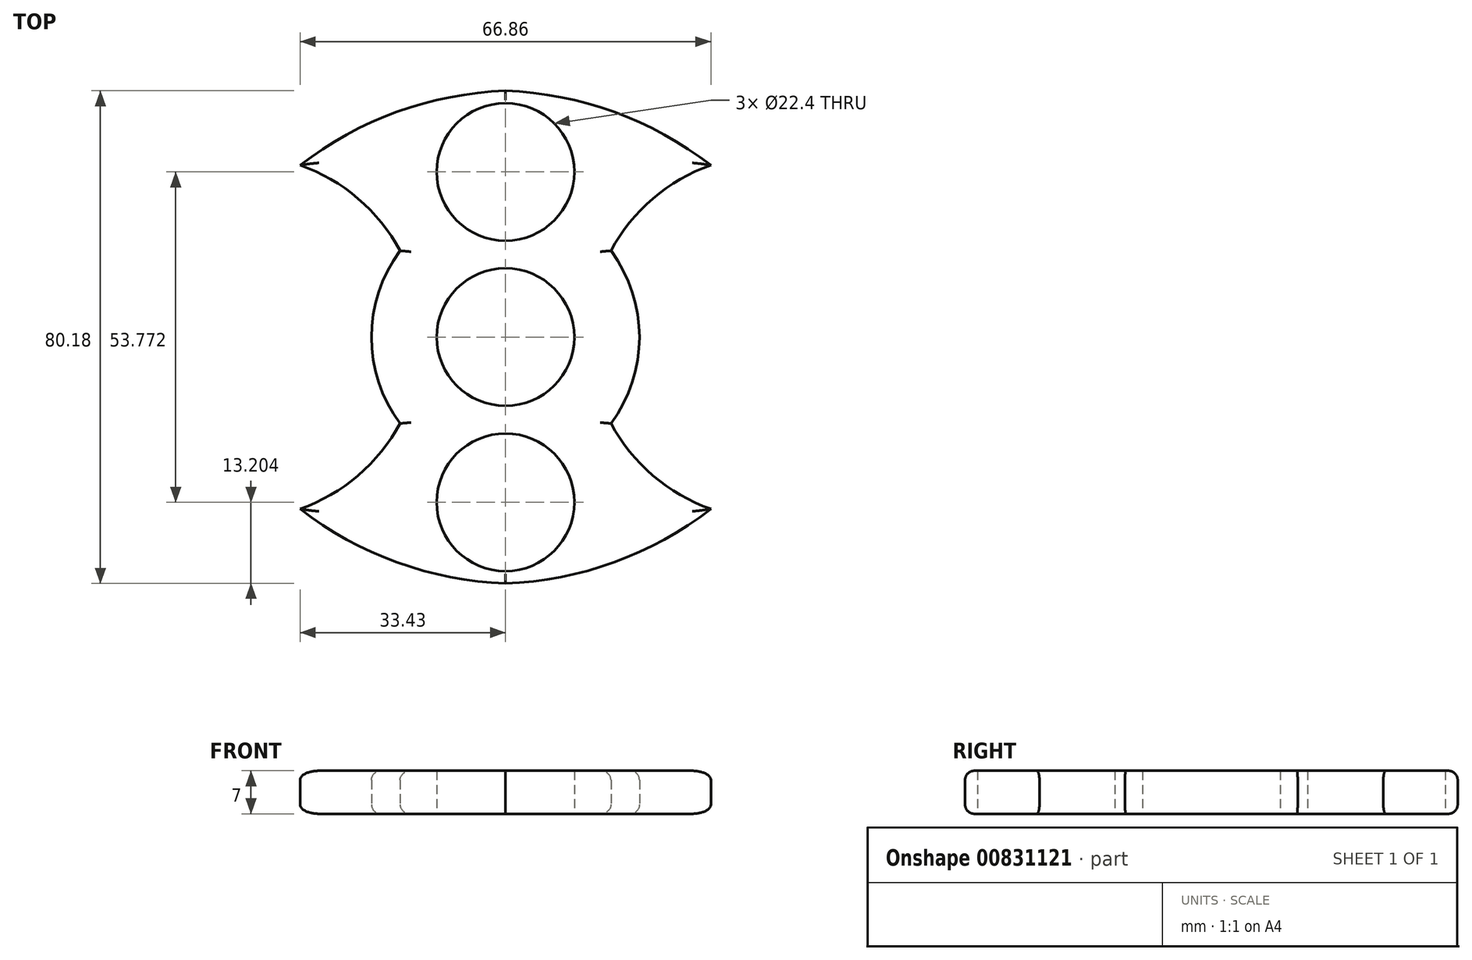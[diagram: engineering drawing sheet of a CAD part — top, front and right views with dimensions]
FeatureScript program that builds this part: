
annotation { "Feature Type Name" : "Feature", "Feature Type Description" : "" }
export const myFeature = defineFeature(function(context is Context, id is Id, definition is map)
    precondition{}
    {
        {
            var Q0;
            Q0=qCreatedBy(makeId("Top.planeOp"),FACE);
            var sketch = newSketch(context, id + "F0", { "sketchPlane" : qUnion([Q0])});
            skCircle(sketch, "E0", {"center": v(0, 0) * mm, "radius": 11.2 * mm});
            skCircle(sketch, "E1", {"center": v(0, 26.89) * mm, "radius": 11.2 * mm});
            skCircle(sketch, "E2.1.1", {"center": v(0, -26.89) * mm, "radius": 11.2 * mm});
            skArc(sketch, "E3", {"start": v(33.43, 27.98) * mm, "mid": v(17.67, 36.66) * mm, "end": v(0, 40.09) * mm});
            skArc(sketch, "E4.MirrorCS", {"start": v(-33.43, 27.98) * mm, "mid": v(-17.67, 36.66) * mm, "end": v(0, 40.09) * mm});
            skArc(sketch, "E5.MirrorCS", {"start": v(-33.43, -27.98) * mm, "mid": v(-17.67, -36.66) * mm, "end": v(0, -40.09) * mm});
            skArc(sketch, "E6.MirrorCS", {"start": v(33.43, -27.98) * mm, "mid": v(17.67, -36.66) * mm, "end": v(0, -40.09) * mm});
            skArc(sketch, "E7", {"start": v(33.43, 27.98) * mm, "mid": v(24, 22.53) * mm, "end": v(17.16, 14.05) * mm});
            skArc(sketch, "E8.MirrorCS", {"start": v(-33.43, 27.98) * mm, "mid": v(-24, 22.53) * mm, "end": v(-17.16, 14.05) * mm});
            skArc(sketch, "E9.trimOffspring", {"start": v(1.21, 40.03) * mm, "mid": v(0, 40.09) * mm, "end": v(-1.21, 40.03) * mm});
            skPoint(sketch, "E10.orphan", {"position": v(10.5, 8) * mm});
            skPoint(sketch, "E11.orphan", {"position": v(-10.5, 8) * mm});
            skPoint(sketch, "E12.start.orphan", {"position": v(11.11, 19.76) * mm});
            skPoint(sketch, "E13.start.orphan", {"position": v(-11.11, 19.76) * mm});
            skPoint(sketch, "E14.orphan", {"position": v(-10.5, -8) * mm});
            skPoint(sketch, "E15.orphan", {"position": v(10.5, -8) * mm});
            skPoint(sketch, "E16.MirrorCS.start.orphan", {"position": v(11.11, -19.76) * mm});
            skPoint(sketch, "E17.MirrorCS.start.orphan", {"position": v(-11.11, -19.76) * mm});
            skArc(sketch, "E18.trimOffspring", {"start": v(-1.21, -40.03) * mm, "mid": v(0, -40.09) * mm, "end": v(1.21, -40.03) * mm});
            skArc(sketch, "E19", {"start": v(17.16, -14.05) * mm, "mid": v(21.8, 0) * mm, "end": v(17.16, 14.05) * mm});
            skArc(sketch, "E20.MirrorCS", {"start": v(-17.16, -14.05) * mm, "mid": v(-21.8, 0) * mm, "end": v(-17.16, 14.05) * mm});
            skArc(sketch, "E21.trimOffspring", {"start": v(17.16, -14.05) * mm, "mid": v(24, -22.53) * mm, "end": v(33.43, -27.98) * mm});
            skArc(sketch, "E22.trimOffspring", {"start": v(-17.16, -14.05) * mm, "mid": v(-24, -22.53) * mm, "end": v(-33.43, -27.98) * mm});
            skSolve(sketch);
        }
        {
            var Q0;
            Q0=makeQuery(id+"F0.imprint","IMPRINT",FACE,{"disambiguationData":[TD([[makeQuery(id+"F0.imprint","IMPRINT",EDGE,{"derivedFrom":sQuery(id+"F0.wireOp",EDGE,"E0")}),-1.0]])]});
            extrude(context, id + "F1", {"entities" : qUnion([Q0]), "depth" : 7 * mm, "offsetDistance" : 25 * mm});
        }
        {
            var Q0;
            Q0=makeQuery(id+"F1.opExtrude","CAP_EDGE",EDGE,{"disambiguationData":[OSD([sQuery(id+"F0.wireOp",EDGE,"E4.MirrorCS")])],"isStart":false});
            var Q1;
            Q1=makeQuery(id+"F1.opExtrude","CAP_EDGE",EDGE,{"disambiguationData":[OSD([sQuery(id+"F0.wireOp",EDGE,"E3")])],"isStart":false});
            var Q2;
            Q2=makeQuery(id+"F1.opExtrude","CAP_EDGE",EDGE,{"disambiguationData":[OSD([sQuery(id+"F0.wireOp",EDGE,"E8.MirrorCS")])],"isStart":false});
            var Q3;
            Q3=makeQuery(id+"F1.opExtrude","CAP_EDGE",EDGE,{"disambiguationData":[OSD([sQuery(id+"F0.wireOp",EDGE,"E20.MirrorCS")])],"isStart":false});
            var Q4;
            Q4=makeQuery(id+"F1.opExtrude","CAP_EDGE",EDGE,{"disambiguationData":[OSD([sQuery(id+"F0.wireOp",EDGE,"E22.trimOffspring")])],"isStart":false});
            var Q5;
            Q5=makeQuery(id+"F1.opExtrude","CAP_EDGE",EDGE,{"disambiguationData":[OSD([sQuery(id+"F0.wireOp",EDGE,"E5.MirrorCS")])],"isStart":false});
            var Q6;
            Q6=makeQuery(id+"F1.opExtrude","CAP_EDGE",EDGE,{"disambiguationData":[OSD([sQuery(id+"F0.wireOp",EDGE,"E6.MirrorCS")])],"isStart":false});
            var Q7;
            Q7=makeQuery(id+"F1.opExtrude","CAP_EDGE",EDGE,{"disambiguationData":[OSD([sQuery(id+"F0.wireOp",EDGE,"E21.trimOffspring")])],"isStart":false});
            var Q8;
            Q8=makeQuery(id+"F1.opExtrude","CAP_EDGE",EDGE,{"disambiguationData":[OSD([sQuery(id+"F0.wireOp",EDGE,"E19")])],"isStart":false});
            var Q9;
            Q9=makeQuery(id+"F1.opExtrude","CAP_EDGE",EDGE,{"disambiguationData":[OSD([sQuery(id+"F0.wireOp",EDGE,"E7")])],"isStart":false});
            fillet(context, id + "F2", {"entities" : qUnion([Q0, Q1, Q2, Q3, Q4, Q5, Q6, Q7, Q8, Q9]), "radius" : 1.5 * mm, "tangentPropagation" : true, "allowEdgeOverflow" : false});
        }
        {
            var Q0;
            Q0=makeQuery(id+"F1.opExtrude","CAP_EDGE",EDGE,{"disambiguationData":[OSD([sQuery(id+"F0.wireOp",EDGE,"E3")])],"isStart":true});
            var Q1;
            Q1=makeQuery(id+"F1.opExtrude","CAP_EDGE",EDGE,{"disambiguationData":[OSD([sQuery(id+"F0.wireOp",EDGE,"E4.MirrorCS")])],"isStart":true});
            var Q2;
            Q2=makeQuery(id+"F1.opExtrude","CAP_EDGE",EDGE,{"disambiguationData":[OSD([sQuery(id+"F0.wireOp",EDGE,"E8.MirrorCS")])],"isStart":true});
            var Q3;
            Q3=makeQuery(id+"F1.opExtrude","CAP_EDGE",EDGE,{"disambiguationData":[OSD([sQuery(id+"F0.wireOp",EDGE,"E20.MirrorCS")])],"isStart":true});
            var Q4;
            Q4=makeQuery(id+"F1.opExtrude","CAP_EDGE",EDGE,{"disambiguationData":[OSD([sQuery(id+"F0.wireOp",EDGE,"E22.trimOffspring")])],"isStart":true});
            var Q5;
            Q5=makeQuery(id+"F1.opExtrude","CAP_EDGE",EDGE,{"disambiguationData":[OSD([sQuery(id+"F0.wireOp",EDGE,"E5.MirrorCS")])],"isStart":true});
            var Q6;
            Q6=makeQuery(id+"F1.opExtrude","CAP_EDGE",EDGE,{"disambiguationData":[OSD([sQuery(id+"F0.wireOp",EDGE,"E6.MirrorCS")])],"isStart":true});
            var Q7;
            Q7=makeQuery(id+"F1.opExtrude","CAP_EDGE",EDGE,{"disambiguationData":[OSD([sQuery(id+"F0.wireOp",EDGE,"E21.trimOffspring")])],"isStart":true});
            var Q8;
            Q8=makeQuery(id+"F1.opExtrude","CAP_EDGE",EDGE,{"disambiguationData":[OSD([sQuery(id+"F0.wireOp",EDGE,"E7")])],"isStart":true});
            var Q9;
            Q9=makeQuery(id+"F1.opExtrude","CAP_EDGE",EDGE,{"disambiguationData":[OSD([sQuery(id+"F0.wireOp",EDGE,"E19")])],"isStart":true});
            fillet(context, id + "F3", {"entities" : qUnion([Q0, Q1, Q2, Q3, Q4, Q5, Q6, Q7, Q8, Q9]), "radius" : 1.5 * mm, "tangentPropagation" : true, "allowEdgeOverflow" : false});
        }
    });
